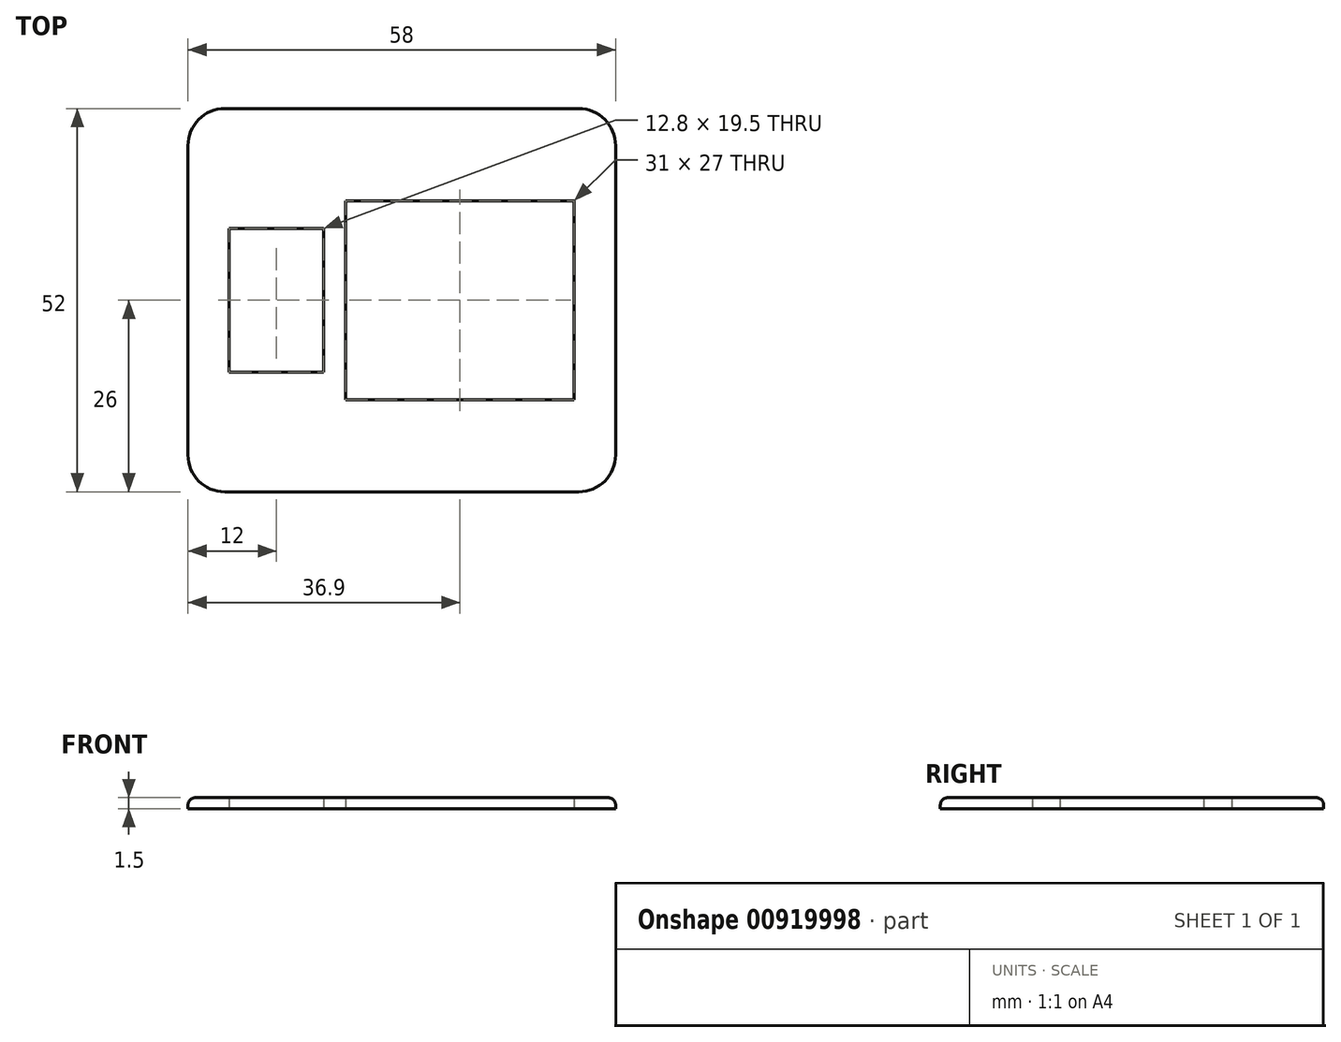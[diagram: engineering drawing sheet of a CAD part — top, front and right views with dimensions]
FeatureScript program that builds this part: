
annotation { "Feature Type Name" : "Feature", "Feature Type Description" : "" }
export const myFeature = defineFeature(function(context is Context, id is Id, definition is map)
    precondition{}
    {
        {
            var Q0;
            Q0=qCreatedBy(makeId("Top.planeOp"),FACE);
            var sketch = newSketch(context, id + "F0", { "sketchPlane" : qUnion([Q0])});
            skLineSegment(sketch, "E0.bottom", {"start": v(24, -26) * mm, "end": v(-24, -26) * mm});
            skLineSegment(sketch, "E0.top", {"start": v(24, 26) * mm, "end": v(-24, 26) * mm});
            skLineSegment(sketch, "E0.left", {"start": v(29, -21) * mm, "end": v(29, 21) * mm});
            skLineSegment(sketch, "E0.right", {"start": v(-29, -21) * mm, "end": v(-29, 21) * mm});
            skPoint(sketch, "E0.middle", {"position": v(0, 0) * mm});
            skLineSegment(sketch, "E1.bottom", {"start": v(23.4, 13.5) * mm, "end": v(-7.6, 13.5) * mm});
            skLineSegment(sketch, "E1.top", {"start": v(23.4, -13.5) * mm, "end": v(-7.6, -13.5) * mm});
            skLineSegment(sketch, "E1.left", {"start": v(23.4, 13.5) * mm, "end": v(23.4, -13.5) * mm});
            skLineSegment(sketch, "E1.right", {"start": v(-7.6, 13.5) * mm, "end": v(-7.6, -13.5) * mm});
            skPoint(sketch, "E2", {"position": v(-7.6, 0) * mm});
            skLineSegment(sketch, "E3.bottom", {"start": v(-10.6, 9.75) * mm, "end": v(-23.4, 9.75) * mm});
            skLineSegment(sketch, "E3.top", {"start": v(-10.6, -9.75) * mm, "end": v(-23.4, -9.75) * mm});
            skLineSegment(sketch, "E3.left", {"start": v(-10.6, 9.75) * mm, "end": v(-10.6, -9.75) * mm});
            skLineSegment(sketch, "E3.right", {"start": v(-23.4, 9.75) * mm, "end": v(-23.4, -9.75) * mm});
            skPoint(sketch, "E4", {"position": v(-23.4, 0) * mm});
            skPoint(sketch, "E5.visualSharp", {"position": v(-29, 26) * mm});
            skArc(sketch, "E5.filletArc", {"start": v(-24, 26) * mm, "mid": v(-27.54, 24.54) * mm, "end": v(-29, 21) * mm});
            skPoint(sketch, "E6.visualSharp", {"position": v(29, 26) * mm});
            skArc(sketch, "E6.filletArc", {"start": v(29, 21) * mm, "mid": v(27.54, 24.54) * mm, "end": v(24, 26) * mm});
            skPoint(sketch, "E7.visualSharp", {"position": v(29, -26) * mm});
            skArc(sketch, "E7.filletArc", {"start": v(24, -26) * mm, "mid": v(27.54, -24.54) * mm, "end": v(29, -21) * mm});
            skPoint(sketch, "E8.visualSharp", {"position": v(-29, -26) * mm});
            skArc(sketch, "E8.filletArc", {"start": v(-29, -21) * mm, "mid": v(-27.54, -24.54) * mm, "end": v(-24, -26) * mm});
            skSolve(sketch);
        }
        {
            var Q0;
            Q0=makeQuery(id+"F0.imprint","IMPRINT",FACE,{"disambiguationData":[TD([[makeQuery(id+"F0.imprint","IMPRINT",EDGE,{"derivedFrom":sQuery(id+"F0.wireOp",EDGE,"E0.bottom")}),-1.0]])]});
            extrude(context, id + "F1", {"entities" : qUnion([Q0]), "depth" : 1.5 * mm, "offsetDistance" : 25 * mm});
        }
        {
            var Q0;
            Q0=makeQuery(id+"F1.opExtrude","CAP_EDGE",EDGE,{"disambiguationData":[OSD([sQuery(id+"F0.wireOp",EDGE,"E0.right")])],"isStart":false});
            fillet(context, id + "F2", {"entities" : qUnion([Q0]), "radius" : 1 * mm, "tangentPropagation" : true, "allowEdgeOverflow" : false});
        }
    });
